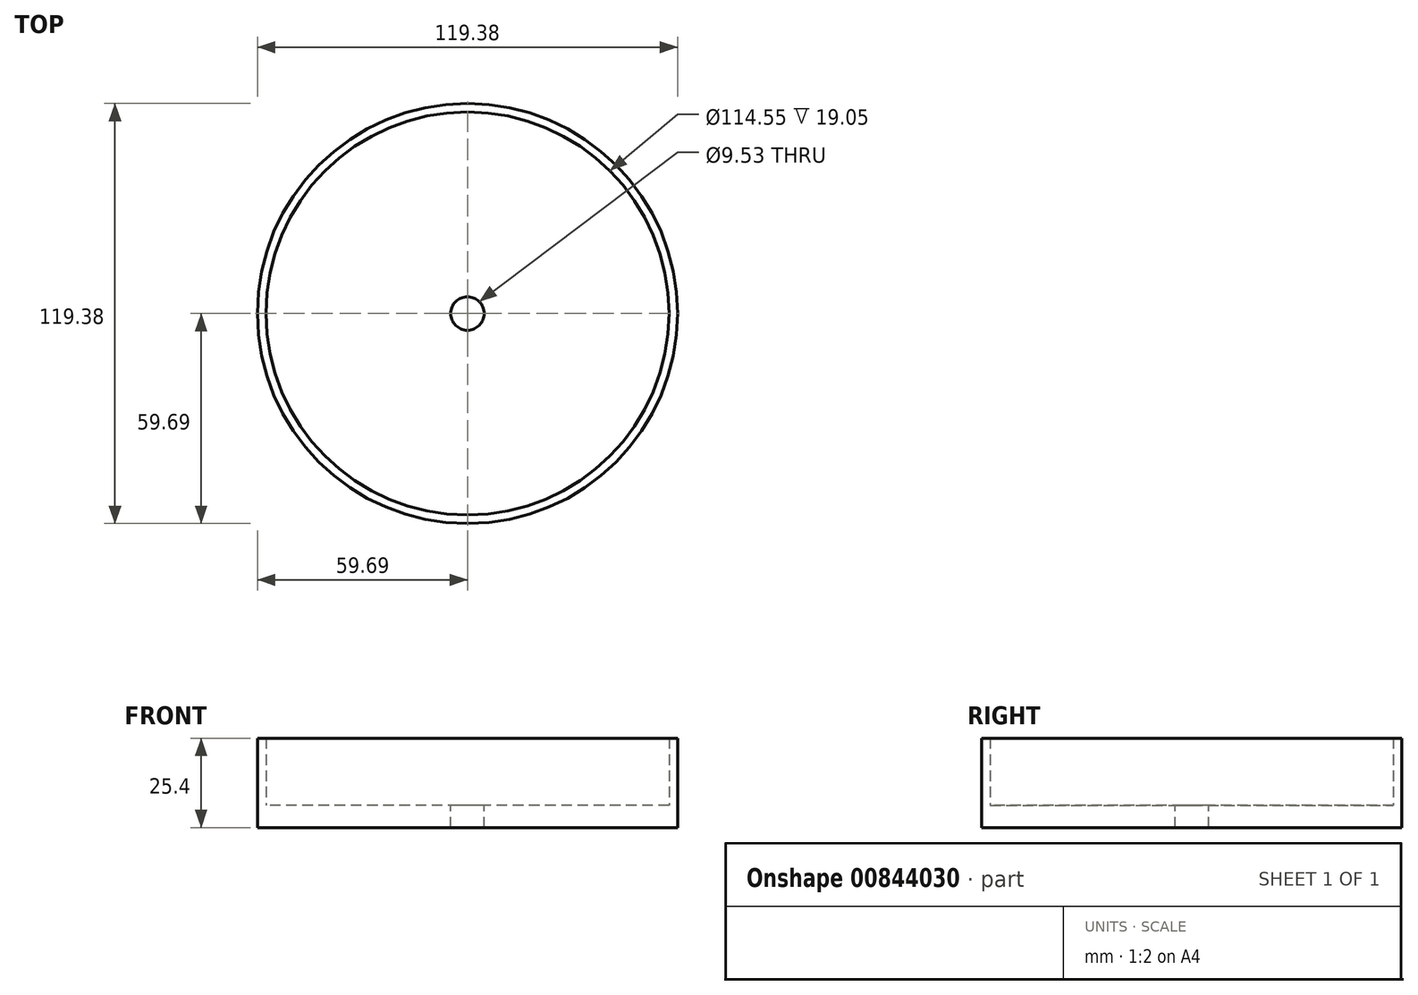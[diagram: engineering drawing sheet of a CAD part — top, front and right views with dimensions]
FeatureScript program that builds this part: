
annotation { "Feature Type Name" : "Feature", "Feature Type Description" : "" }
export const myFeature = defineFeature(function(context is Context, id is Id, definition is map)
    precondition{}
    {
        {
            var Q0;
            Q0=qCreatedBy(makeId("Top.planeOp"),FACE);
            var sketch = newSketch(context, id + "F0", { "sketchPlane" : qUnion([Q0])});
            skCircle(sketch, "E0", {"center": v(0, 0) * mm, "radius": 59.7 * mm});
            skSolve(sketch);
        }
        {
            var Q0;
            Q0 = qSketchRegion(id + "F0", true);
            var Q1;
            Q1 = qSketchRegion(id + "F2", true);
            extrude(context, id + "F1", {"entities" : qUnion([Q0, Q1]), "depth" : 6.35 * mm, "offsetDistance" : 25.4 * mm});
        }
        {
            var Q0;
            Q0=makeQuery(id+"F1.opExtrude","CAP_FACE",FACE,{"disambiguationData":[OSD([sQuery(id+"F0.wireOp",EDGE,"E0")])],"isStart":false});
            var sketch = newSketch(context, id + "F2", { "sketchPlane" : qUnion([Q0])});
            skCircle(sketch, "E1", {"center": v(0, 0) * mm, "radius": 57.28 * mm});
            skSolve(sketch);
        }
        {
            var Q0;
            Q0=makeQuery(id+"F2.imprint","IMPRINT",FACE,{"disambiguationData":[TD([[makeQuery(id+"F2.imprint","IMPRINT",EDGE,{"derivedFrom":sQuery(id+"F2.wireOp",EDGE,"E1")}),-1.0]])]});
            extrude(context, id + "F3", {"entities" : qUnion([Q0]), "operationType" : NewBodyOperationType.ADD, "depth" : 19.05 * mm, "offsetDistance" : 25.4 * mm});
        }
        {
            var Q0;
            Q0=makeQuery(id+"F1.opExtrude","CAP_FACE",FACE,{"disambiguationData":[OSD([sQuery(id+"F0.wireOp",EDGE,"E0")])],"isStart":false});
            var sketch = newSketch(context, id + "F4", { "sketchPlane" : qUnion([Q0])});
            skCircle(sketch, "E2", {"center": v(0, 0) * mm, "radius": 4.76 * mm});
            skSolve(sketch);
        }
        {
            var Q0;
            Q0 = qSketchRegion(id + "F4", true);
            extrude(context, id + "F5", {"entities" : qUnion([Q0]), "operationType" : NewBodyOperationType.REMOVE, "oppositeDirection" : true, "depth" : 25.4 * mm, "offsetDistance" : 25.4 * mm});
        }
    });
